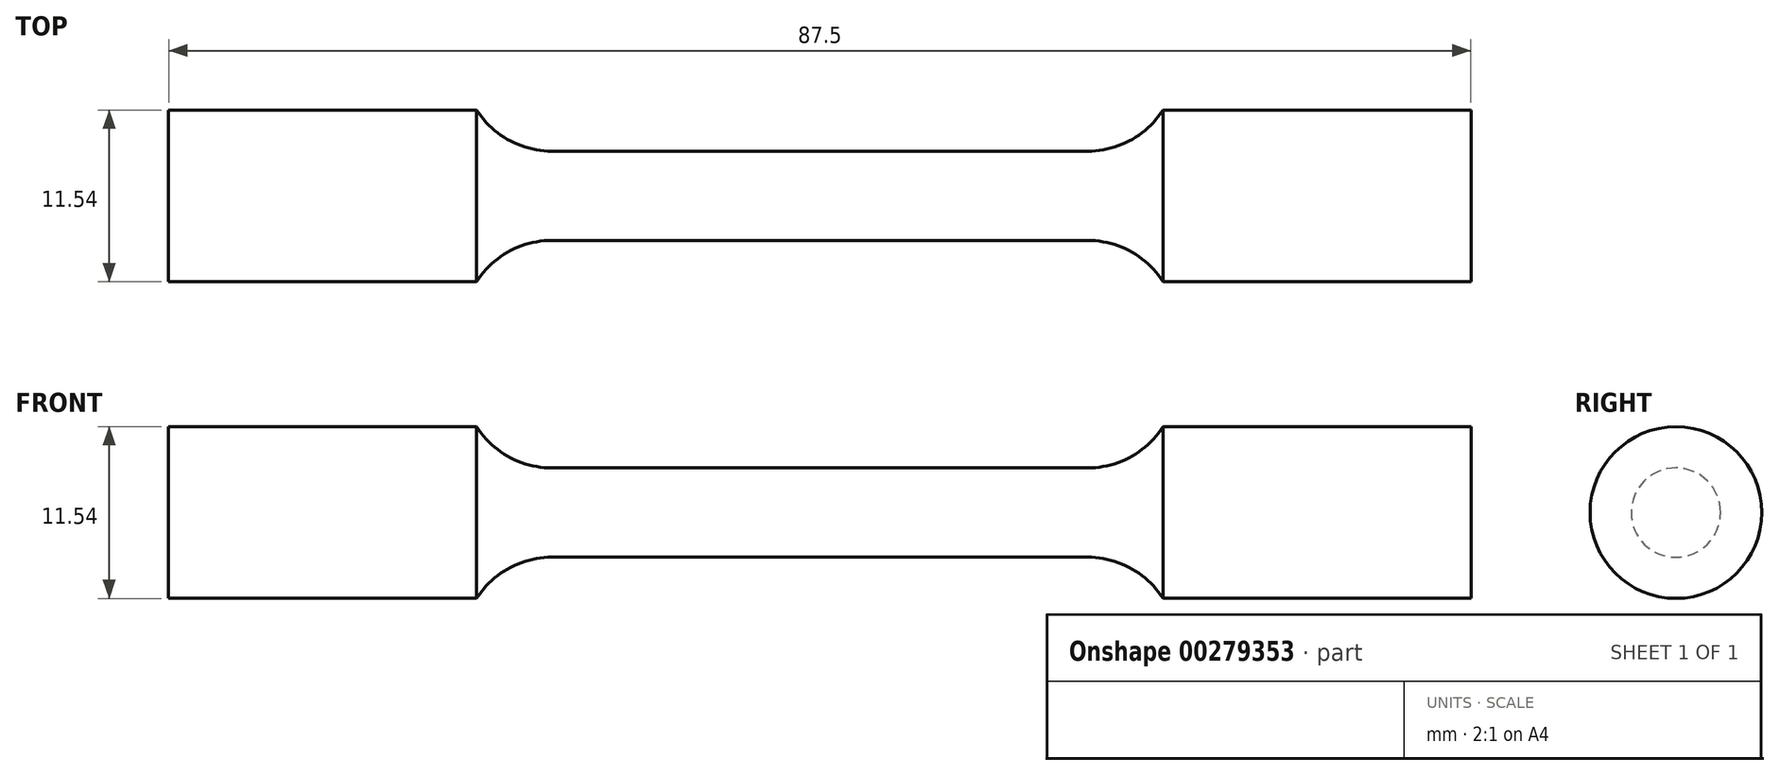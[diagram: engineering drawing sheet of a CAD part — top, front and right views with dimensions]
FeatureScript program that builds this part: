
annotation { "Feature Type Name" : "Feature", "Feature Type Description" : "" }
export const myFeature = defineFeature(function(context is Context, id is Id, definition is map)
    precondition{}
    {
        {
            var Q0;
            Q0=qCreatedBy(makeId("Front.planeOp"),FACE);
            var sketch = newSketch(context, id + "F0", { "sketchPlane" : qUnion([Q0])});
            skLineSegment(sketch, "E0", {"start": v(0, 3) * mm, "end": v(18, 3) * mm});
            skArc(sketch, "E1", {"start": v(18, 3) * mm, "mid": v(20.88, 3.74) * mm, "end": v(23.06, 5.77) * mm});
            skLineSegment(sketch, "E2", {"start": v(23.06, 5.77) * mm, "end": v(43.75, 5.77) * mm});
            skLineSegment(sketch, "E3", {"start": v(43.75, 5.77) * mm, "end": v(43.75, 0) * mm});
            skLineSegment(sketch, "E4.MirrorCS", {"start": v(0, 3) * mm, "end": v(-18, 3) * mm});
            skLineSegment(sketch, "E5.MirrorCS", {"start": v(-23.06, 5.77) * mm, "end": v(-43.75, 5.77) * mm});
            skArc(sketch, "E6.MirrorCS", {"start": v(-18, 3) * mm, "mid": v(-20.88, 3.74) * mm, "end": v(-23.06, 5.77) * mm});
            skLineSegment(sketch, "E7.MirrorCS", {"start": v(-43.75, 5.77) * mm, "end": v(-43.75, 0) * mm});
            skLineSegment(sketch, "E8", {"start": v(-43.75, 0) * mm, "end": v(43.75, 0) * mm});
            skSolve(sketch);
        }
        {
            var Q0;
            Q0 = qSketchRegion(id + "F0", true);
            var Q1;
            Q1=sQuery(id+"F0.wireOp",EDGE,"E8");
            revolve(context, id + "F1", {"entities" : qUnion([Q0]), "axis" : qUnion([Q1]), "revolveType" : RevolveType.FULL});
        }
    });
